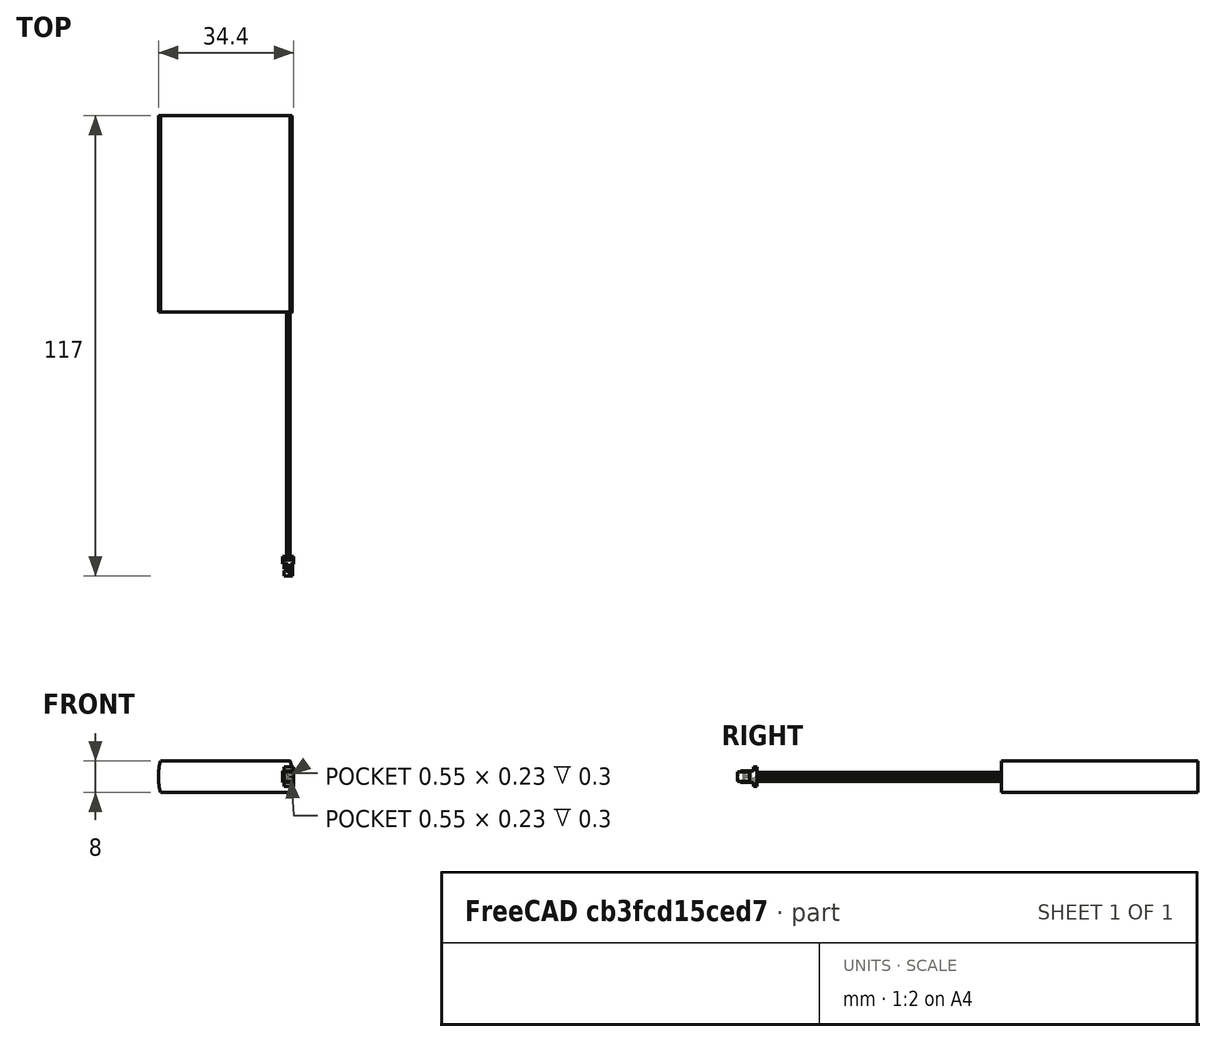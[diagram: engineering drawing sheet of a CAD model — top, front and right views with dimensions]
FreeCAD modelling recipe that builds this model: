
FCSTD DOCUMENT  (FreeCAD 2021.519R24301 +3652 (Git))
Label: ASR00073_1500mAh
License: Other
objects: TechDraw::DrawViewDimension×4, Sketcher::SketchObject×3, PartDesign::Pad×3, TechDraw::DrawViewPart×2, TechDraw::DrawViewAnnotation×2, PartDesign::Pocket×1, PartDesign::Mirrored×1, PartDesign::Body×1, Part::Feature×1, Part::MultiFuse×1, TechDraw::DrawSVGTemplate×1, TechDraw::DrawPage×1, Mesh::Feature×1
note: 21 computed .brp shape members not serialized (recipe doc carries the construction recipe); baked Part::Feature solids carry a one-line shape summary decoded from their .brp

FEATURE [Sketcher::SketchObject] Sketch
  FullyConstrained = true
  MapMode = 5
  Support = -> [XY_Plane]
  sketch-geometry (4):
    g0: LineSegment StartX=-17 StartY=25 StartZ=0 EndX=17 EndY=25 EndZ=0
    g1: LineSegment StartX=17 StartY=25 StartZ=0 EndX=17 EndY=-25 EndZ=0
    g2: LineSegment StartX=17 StartY=-25 StartZ=0 EndX=-17 EndY=-25 EndZ=0
    g3: LineSegment StartX=-17 StartY=-25 StartZ=0 EndX=-17 EndY=25 EndZ=0
  constraints (10):
    c: Coincident(g0,g1)
    c: Coincident(g1,g2)
    c: Coincident(g2,g3)
    c: Coincident(g3,g0)
    c: Horizontal(g2)
    c: Vertical(g1)
    c: Symmetric(g0,g2,g-1)
    c: Symmetric(g0,g0,g-2)
    c: DistanceX(g0,g0) = 34
    c: DistanceY(g3,g3) = 50
FEATURE [PartDesign::Pad] Pad
  ClaimChildren = false
  Direction = (1,1,1)
  Fit = 0
  FitJoin = 0
  InnerFit = 0
  InnerFitJoin = 0
  InnerTaperAngle = 0
  InnerTaperAngleRev = 0
  Length = 8
  Length2 = 100
  Midplane = true
  NewSolid = false
  Profile = -> Sketch
  Suppress = false
  Type = 0
FEATURE [Sketcher::SketchObject] Sketch001
  ExternalGeometry = -> [Pad]
  FullyConstrained = true
  MapMode = 5
  Placement = pos=(0,25,0) rot=(0,0.707107,0.707107;3.14159rad)
  Support = -> [Pad]
  sketch-geometry (5):
    g0: ArcOfCircle CenterX=-0.75 CenterY=-1.6e-15 CenterZ=0 NormalX=0 NormalY=0 NormalZ=1 AngleXU=0 Radius=16.25 StartAngle=2.89288 EndAngle=3.3903
    g1: LineSegment [constr] StartX=-16.5 StartY=-4 StartZ=0 EndX=-16.5 EndY=4 EndZ=0
    g2: LineSegment StartX=-16.5 StartY=-4 StartZ=0 EndX=-18 EndY=-4 EndZ=0
    g3: LineSegment StartX=-16.5 StartY=4 StartZ=0 EndX=-18 EndY=4 EndZ=0
    g4: LineSegment StartX=-18 StartY=4 StartZ=0 EndX=-18 EndY=-4 EndZ=0
  constraints (15):
    c: PointOnObject(g0,g-5)
    c: PointOnObject(g0,g-4)
    c: Tangent(g0,g-3)
    c: Coincident(g1,g0)
    c: Coincident(g1,g0)
    c: Vertical(g1)
    c: Coincident(g2,g0)
    c: Horizontal(g2)
    c: Coincident(g3,g0)
    c: Horizontal(g3)
    c: Coincident(g4,g3)
    c: Coincident(g4,g2)
    c: Vertical(g4)
    c: DistanceX(g3,g-4) = 1
    c: DistanceX(g-4,g0) = 0.5
FEATURE [PartDesign::Pocket] Pocket
  BaseFeature = -> Pad
  ClaimChildren = false
  Fit = 0
  FitJoin = 0
  InnerFit = 0
  InnerFitJoin = 0
  InnerTaperAngle = 0
  InnerTaperAngleRev = 0
  Length = 5
  Length2 = 100
  NewSolid = false
  Profile = -> Sketch001
  Suppress = false
  Type = 1
FEATURE [PartDesign::Mirrored] Mirrored
  BaseFeature = -> Pocket
  CopyShape = true
  MirrorPlane = -> Sketch001 [V_Axis]
  NewSolid = false
  OriginalSubs = -> [Pocket]
  Originals = -> [Pocket]
  ParallelTransform = true
  SubTransform = true
  Suppress = false
FEATURE [PartDesign::Pad] Pad001
  BaseFeature = -> Mirrored
  ClaimChildren = false
  Direction = (1,1,1)
  Fit = 0
  FitJoin = 0
  InnerFit = 0
  InnerFitJoin = 0
  InnerTaperAngle = 0
  InnerTaperAngleRev = 0
  Length = 7.85
  Length2 = 100
  NewSolid = false
  Profile = -> Mirrored [Face8]
  Reversed = true
  Suppress = false
  Type = 0
FEATURE [Sketcher::SketchObject] Sketch002
  ExternalGeometry = -> [Pad001]
  FullyConstrained = true
  MapMode = 5
  Placement = pos=(0,-25,0) rot=(1,0,0;1.5708rad)
  Support = -> [Pad001]
  sketch-geometry (6):
    g0: Circle CenterX=16 CenterY=-0.7 CenterZ=0 NormalX=0 NormalY=0 NormalZ=1 AngleXU=0 Radius=0.45
    g1: Circle CenterX=16 CenterY=0.7 CenterZ=0 NormalX=0 NormalY=0 NormalZ=1 AngleXU=0 Radius=0.45
    g2: LineSegment [constr] StartX=16 StartY=0.7 StartZ=0 EndX=16 EndY=-0.7 EndZ=0
    g3: GeomPoint [constr] X=16 Y=-0.25 Z=0
    g4: GeomPoint [constr] X=16 Y=0.25 Z=0
    g5: LineSegment [constr] StartX=16 StartY=-0.7 StartZ=0 EndX=16.45 EndY=-0.7 EndZ=0
  constraints (13):
    c: Coincident(g2,g1)
    c: Coincident(g2,g0)
    c: Equal(g0,g1)
    c: Diameter(g0) = 0.9
    c: Symmetric(g0,g1,g-1)
    c: PointOnObject(g3,g2)
    c: PointOnObject(g4,g1)
    c: Symmetric(g3,g4,g-1)
    c: DistanceY(g-3,g3) = 3.75
    c: Coincident(g5,g0)
    c: PointOnObject(g5,g0)
    c: Horizontal(g5)
    c: DistanceX(g5,g-3) = 0.05
FEATURE [PartDesign::Pad] Pad002
  BaseFeature = -> Pad001
  ClaimChildren = false
  Direction = (1,1,1)
  Fit = 0
  FitJoin = 0
  InnerFit = 0
  InnerFitJoin = 0
  InnerTaperAngle = 0
  InnerTaperAngleRev = 0
  Length = 62
  Length2 = 100
  NewSolid = false
  Profile = -> Sketch002
  Suppress = false
  Type = 0
FEATURE [PartDesign::Body] Body
  AutoGroupSolids = false
  ExportMode = 0
  Group = -> [Sketch,Pad,Sketch001,Pocket,Mirrored,Pad001,Sketch002,Pad002]
  Origin = -> Origin
  Tip = -> Pad002
  _ExportChildren = -> [Pad,Pocket,Mirrored,Pad001,Pad002]
  _GroupVersion = 1
FEATURE [Part::Feature] Solid  label="Body007"
  Placement = pos=(14.7155,-89,1.28e-14) rot=(0,0,1;0rad)
  shape: bbox 2.9 x 5 x 4.94 mm, 60 faces (baked)
FEATURE [Part::MultiFuse] Fusion
  Shapes = -> [Body,Solid]
FEATURE [TechDraw::DrawSVGTemplate] Template
  Height = 210
  Orientation = 1
  Width = 297
FEATURE [TechDraw::DrawViewPart] View
  CoarseView = false
  Direction = (0,0,1)
  Focus = 100
  HardHidden = false
  IsoCount = 0
  IsoHidden = false
  IsoVisible = false
  LockPosition = false
  Perspective = false
  Rotation = 180
  Scale = 0.935
  ScaleType = 0
  SeamHidden = false
  SeamVisible = true
  SmoothHidden = false
  SmoothVisible = true
  Source = -> [Fusion]
  X = 178.5
  XDirection = (1,0,0)
  Y = 105
FEATURE [TechDraw::DrawViewPart] View001
  CoarseView = false
  Direction = (-1,0,0)
  Focus = 100
  HardHidden = false
  IsoCount = 0
  IsoHidden = false
  IsoVisible = false
  LockPosition = false
  Perspective = false
  Rotation = 90
  Scale = 0.935
  ScaleType = 0
  SeamHidden = false
  SeamVisible = true
  SmoothHidden = false
  SmoothVisible = true
  Source = -> [Fusion]
  X = 118.5
  XDirection = (0,-1,0)
  Y = 105
FEATURE [TechDraw::DrawViewAnnotation] Annotation
  Font = MS Shell Dlg 2
  LineSpace = 80
  LockPosition = false
  MaxWidth = -1
  Rotation = 0
  ScaleType = 0
  Text = SIDE VIEW
  TextSize = 6
  TextStyle = 0
  X = 118.5
  Y = 162
FEATURE [TechDraw::DrawViewAnnotation] Annotation001
  Font = MS Shell Dlg 2
  LineSpace = 80
  LockPosition = false
  MaxWidth = -1
  Rotation = 0
  ScaleType = 0
  Text = TOP VIEW
  TextSize = 6
  TextStyle = 0
  X = 178.5
  Y = 162
FEATURE [TechDraw::DrawViewDimension] Dimension
  Arbitrary = false
  ArbitraryTolerances = false
  EqualTolerance = true
  FormatSpec = %.1f
  FormatSpecOverTolerance = %+.1f
  FormatSpecUnderTolerance = %+.1f
  Inverted = false
  LockPosition = false
  MeasureType = 1
  OverTolerance = 0.5
  References2D = -> [View001]
  Rotation = 0
  ScaleType = 0
  TheoreticalExact = false
  Type = 1
  UnderTolerance = -0.5
  X = -32
  Y = -59
FEATURE [TechDraw::DrawViewDimension] Dimension001
  Arbitrary = false
  ArbitraryTolerances = false
  EqualTolerance = true
  FormatSpec = %.1f
  FormatSpecOverTolerance = %+.1f
  FormatSpecUnderTolerance = %+.1f
  Inverted = false
  LockPosition = false
  MeasureType = 1
  OverTolerance = 2
  References2D = -> [View]
  Rotation = 0
  ScaleType = 0
  TheoreticalExact = false
  Type = 1
  UnderTolerance = -2
  X = 34.187
  Y = -59
FEATURE [TechDraw::DrawViewDimension] Dimension002
  Arbitrary = false
  ArbitraryTolerances = false
  EqualTolerance = true
  FormatSpec = %.1f
  FormatSpecOverTolerance = %+.1f
  FormatSpecUnderTolerance = %+.1f
  Inverted = false
  LockPosition = false
  MeasureType = 1
  OverTolerance = 3
  References2D = -> [View]
  Rotation = 0
  ScaleType = 0
  TheoreticalExact = false
  Type = 2
  UnderTolerance = -3
  X = -33
  Y = -30.2
FEATURE [TechDraw::DrawViewDimension] Dimension003
  Arbitrary = false
  ArbitraryTolerances = false
  EqualTolerance = true
  FormatSpec = %.1f
  FormatSpecOverTolerance = %+.1f
  FormatSpecUnderTolerance = %+.1f
  Inverted = false
  LockPosition = false
  MeasureType = 1
  OverTolerance = 5
  References2D = -> [View]
  Rotation = 0
  ScaleType = 0
  TheoreticalExact = false
  Type = 2
  UnderTolerance = -5
  X = -33
  Y = 22.0375
FEATURE [TechDraw::DrawPage] Page
  KeepUpdated = true
  NextBalloonIndex = 1
  ProjectionType = 0
  Template = -> Template
  Views = -> [View,View001,Annotation,Annotation001,Dimension,Dimension001,Dimension002,Dimension003]
FEATURE [Mesh::Feature] Mesh  label="Fusion (Meshed)"
